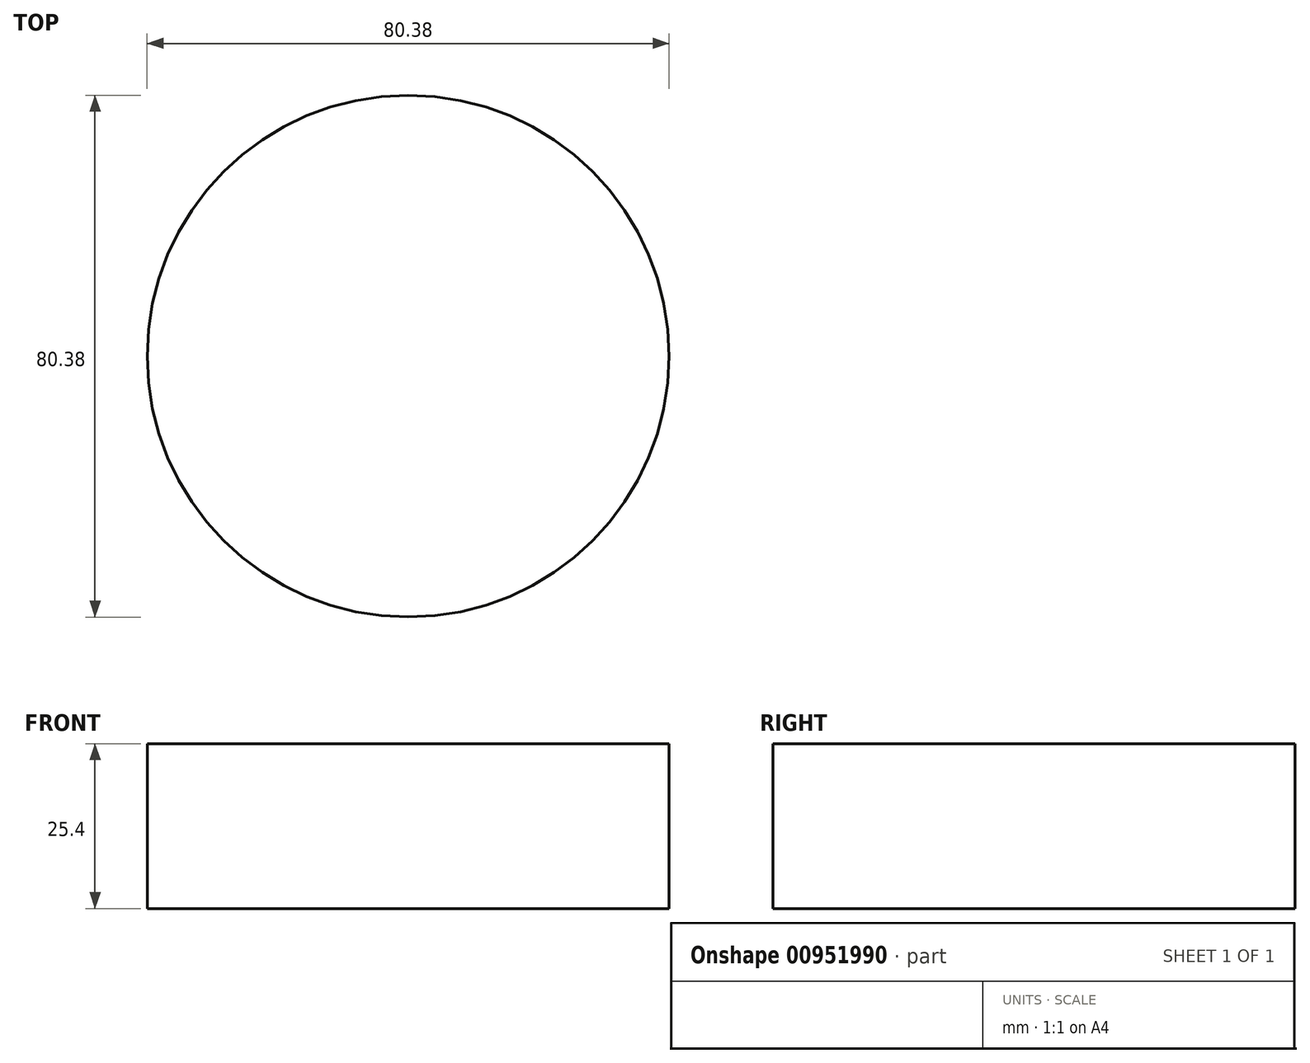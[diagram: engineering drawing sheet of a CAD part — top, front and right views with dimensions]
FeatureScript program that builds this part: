
annotation { "Feature Type Name" : "Feature", "Feature Type Description" : "" }
export const myFeature = defineFeature(function(context is Context, id is Id, definition is map)
    precondition{}
    {
        {
            var Q0;
            Q0=qCreatedBy(makeId("Top.planeOp"),FACE);
            var sketch = newSketch(context, id + "F0", { "sketchPlane" : qUnion([Q0])});
            skCircle(sketch, "E0", {"center": v(0, 0) * mm, "radius": 40.19 * mm});
            skSolve(sketch);
        }
        {
            var Q0;
            Q0 = qSketchRegion(id + "F0", true);
            extrude(context, id + "F1", {"entities" : qUnion([Q0]), "depth" : 25.4 * mm, "offsetDistance" : 25.4 * mm});
        }
    });
